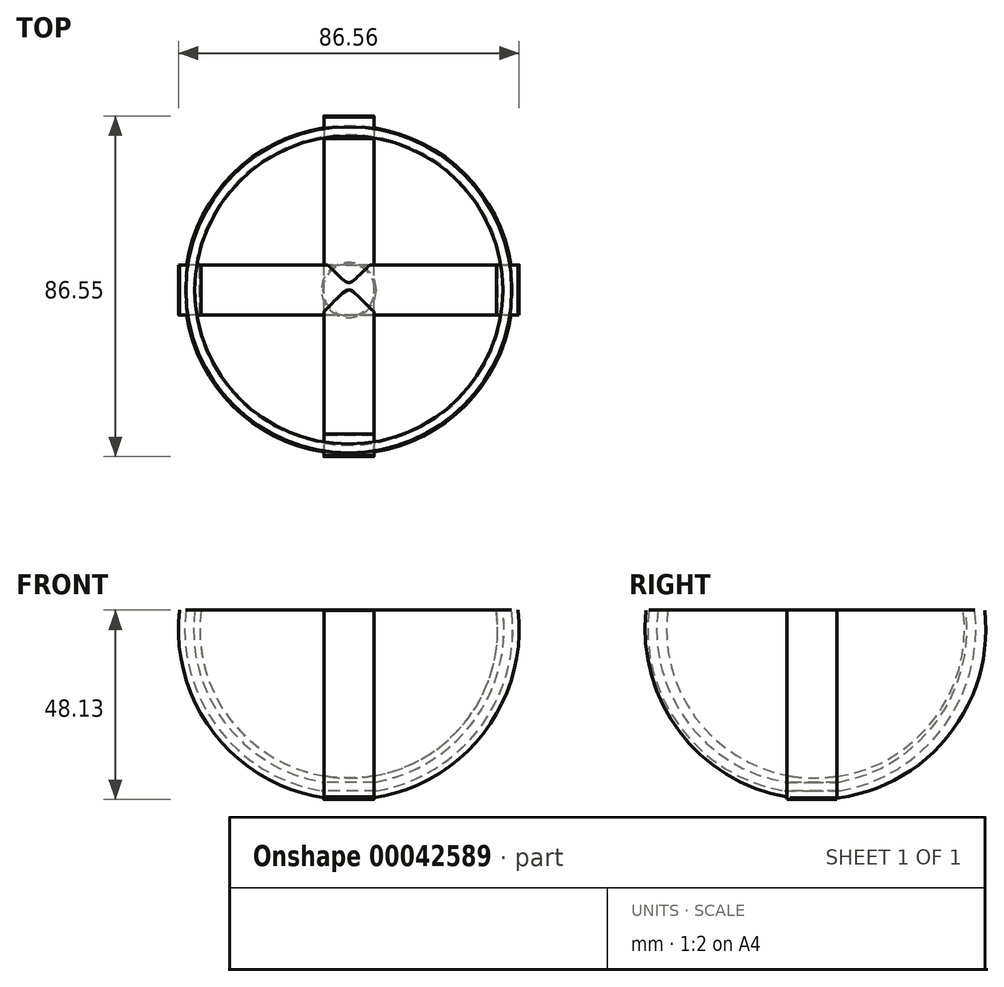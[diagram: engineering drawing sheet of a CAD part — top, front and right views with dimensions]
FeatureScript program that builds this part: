
annotation { "Feature Type Name" : "Feature", "Feature Type Description" : "" }
export const myFeature = defineFeature(function(context is Context, id is Id, definition is map)
    precondition{}
    {
        {
            var Q0;
            Q0=qCreatedBy(makeId("Front.planeOp"),FACE);
            var sketch = newSketch(context, id + "F0", { "sketchPlane" : qUnion([Q0])});
            skArc(sketch, "E0", {"start": v(-43, 48.1) * mm, "mid": v(0, 0) * mm, "end": v(43, 48.1) * mm});
            skArc(sketch, "E1.0", {"start": v(-37.54, 48.1) * mm, "mid": v(0, 5.43) * mm, "end": v(37.54, 48.1) * mm});
            skLineSegment(sketch, "E2", {"start": v(43, 48.1) * mm, "end": v(37.54, 48.1) * mm});
            skLineSegment(sketch, "E3.trimOffspring", {"start": v(-37.54, 48.1) * mm, "end": v(-43, 48.1) * mm});
            skSolve(sketch);
        }
        {
            var Q0;
            Q0=makeQuery(id+"F0.imprint","IMPRINT",FACE,{"disambiguationData":[TD([[makeQuery(id+"F0.imprint","IMPRINT",EDGE,{"derivedFrom":sQuery(id+"F0.wireOp",EDGE,"E0")}),1.0]])]});
            extrude(context, id + "F1", {"entities" : qUnion([Q0]), "depth" : 6.35 * mm, "hasSecondDirection" : true, "secondDirectionOppositeDirection" : true, "secondDirectionDepth" : 6.35 * mm});
        }
        {
            var Q0;
            Q0=qCreatedBy(makeId("Right.planeOp"),FACE);
            var sketch = newSketch(context, id + "F2", { "sketchPlane" : qUnion([Q0])});
            skArc(sketch, "E4", {"start": v(-42.08, 48.1) * mm, "mid": v(0.93, 0) * mm, "end": v(43.93, 48.1) * mm});
            skArc(sketch, "E5.0", {"start": v(-36.61, 48.1) * mm, "mid": v(0.93, 5.42) * mm, "end": v(38.46, 48.1) * mm});
            skLineSegment(sketch, "E6", {"start": v(43.93, 48.1) * mm, "end": v(38.46, 48.1) * mm});
            skLineSegment(sketch, "E7.trimOffspring", {"start": v(-36.61, 48.1) * mm, "end": v(-42.08, 48.1) * mm});
            skSolve(sketch);
        }
        {
            var Q0;
            Q0 = qSketchRegion(id + "F2", true);
            extrude(context, id + "F3", {"entities" : qUnion([Q0]), "operationType" : NewBodyOperationType.ADD, "depth" : 6.35 * mm, "hasSecondDirection" : true, "secondDirectionOppositeDirection" : true, "secondDirectionDepth" : 6.35 * mm});
        }
        {
            var Q0;
            Q0=qCreatedBy(makeId("Front.planeOp"),FACE);
            var sketch = newSketch(context, id + "F4", { "sketchPlane" : qUnion([Q0])});
            skArc(sketch, "E8.0", {"start": v(-39.14, 48.12) * mm, "mid": v(-31.64, 19.74) * mm, "end": v(-6.62, 4.4) * mm});
            skArc(sketch, "E9.0", {"start": v(-41.4, 48.12) * mm, "mid": v(-33.36, 18.29) * mm, "end": v(-7, 2.19) * mm});
            skLineSegment(sketch, "E10", {"start": v(-39.14, 48.12) * mm, "end": v(-41.4, 48.12) * mm});
            skLineSegment(sketch, "E11", {"start": v(-6.62, 4.4) * mm, "end": v(0, 4.4) * mm});
            skLineSegment(sketch, "E12", {"start": v(0, 4.4) * mm, "end": v(0, 2.19) * mm});
            skLineSegment(sketch, "E13", {"start": v(0, 2.19) * mm, "end": v(-7, 2.19) * mm});
            skSolve(sketch);
        }
        {
            var Q0;
            Q0 = qSketchRegion(id + "F4", true);
            var Q1;
            Q1=sQuery(id+"F4.wireOp",EDGE,"E12");
            revolve(context, id + "F5", {"entities" : qUnion([Q0]), "axis" : qUnion([Q1]), "revolveType" : RevolveType.FULL});
        }
    });
